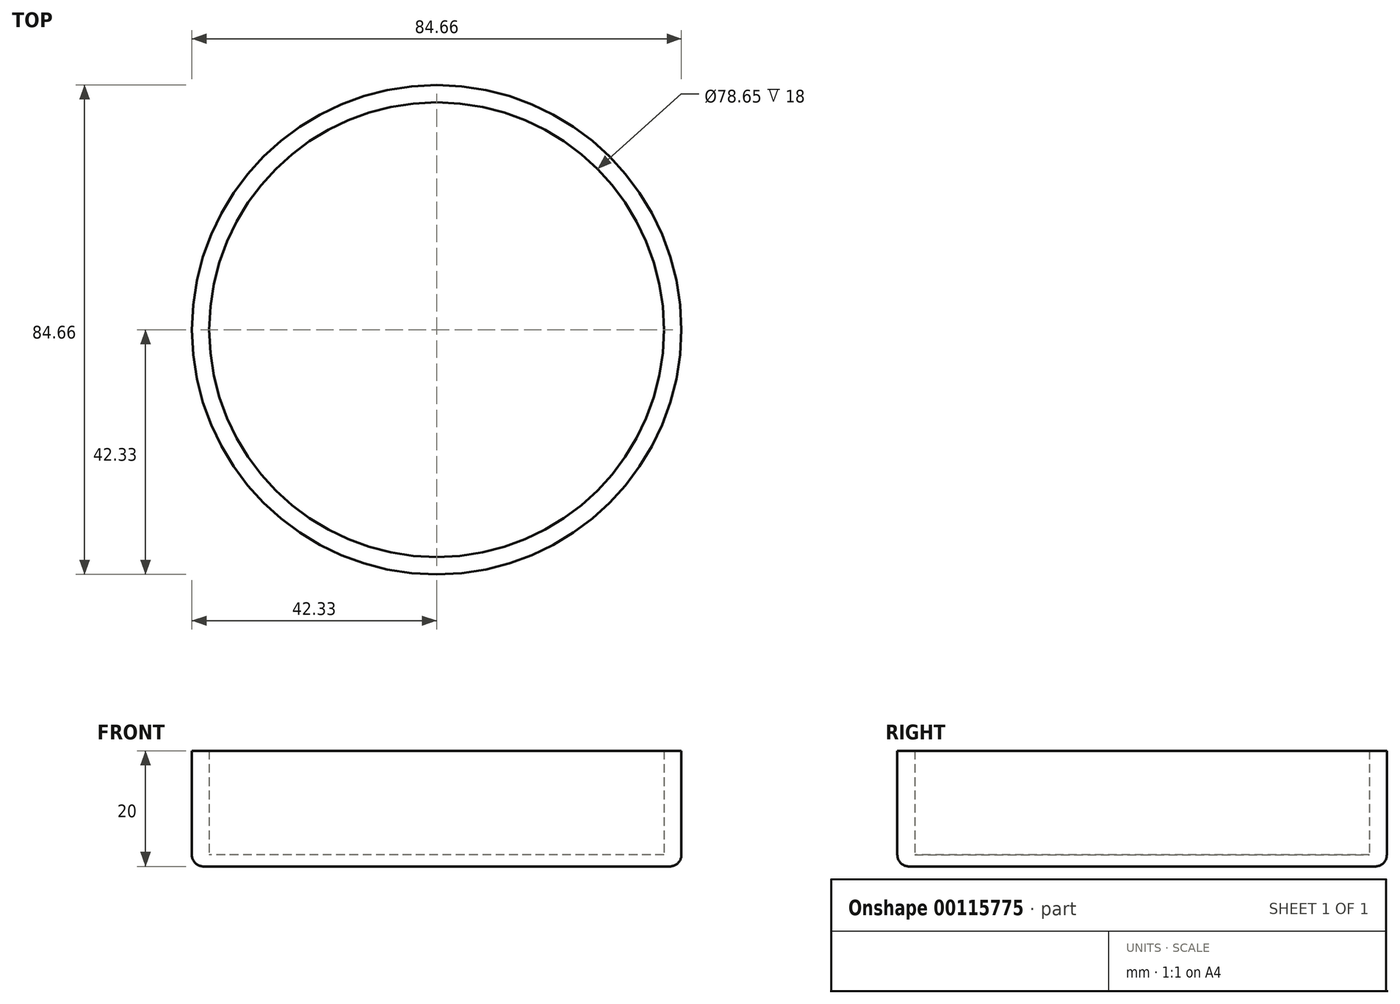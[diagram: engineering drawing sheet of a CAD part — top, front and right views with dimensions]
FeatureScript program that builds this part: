
annotation { "Feature Type Name" : "Feature", "Feature Type Description" : "" }
export const myFeature = defineFeature(function(context is Context, id is Id, definition is map)
    precondition{}
    {
        {
            var Q0;
            Q0=qCreatedBy(makeId("Top.planeOp"),FACE);
            var sketch = newSketch(context, id + "F0", { "sketchPlane" : qUnion([Q0])});
            skCircle(sketch, "E0", {"center": v(0, 0) * mm, "radius": 42.33 * mm});
            skSolve(sketch);
        }
        {
            var Q0;
            Q0=makeQuery(id+"F0.imprint","IMPRINT",FACE,{"disambiguationData":[TD([[makeQuery(id+"F0.imprint","IMPRINT",EDGE,{"derivedFrom":sQuery(id+"F0.wireOp",EDGE,"E0")}),1.0]])]});
            extrude(context, id + "F1", {"entities" : qUnion([Q0]), "depth" : 2 * mm});
        }
        {
            var Q0;
            Q0=makeQuery(id+"F1.opExtrude","CAP_FACE",FACE,{"disambiguationData":[OSD([sQuery(id+"F0.wireOp",EDGE,"E0")])],"isStart":false});
            var sketch = newSketch(context, id + "F2", { "sketchPlane" : qUnion([Q0])});
            skCircle(sketch, "E1", {"center": v(0, 0) * mm, "radius": 42.33 * mm});
            skCircle(sketch, "E2", {"center": v(0, 0) * mm, "radius": 39.33 * mm});
            skSolve(sketch);
        }
        {
            var Q0;
            Q0=makeQuery(id+"F2.imprint","IMPRINT",FACE,{"disambiguationData":[TD([[makeQuery(id+"F2.imprint","IMPRINT",EDGE,{"derivedFrom":sQuery(id+"F2.wireOp",EDGE,"E1")}),1.0]])]});
            extrude(context, id + "F3", {"entities" : qUnion([Q0]), "operationType" : NewBodyOperationType.ADD, "depth" : 18 * mm});
        }
        {
            var Q0;
            Q0=makeQuery(id+"F1.opExtrude","CAP_EDGE",EDGE,{"disambiguationData":[OSD([sQuery(id+"F0.wireOp",EDGE,"E0")])],"isStart":true});
            fillet(context, id + "F4", {"entities" : qUnion([Q0]), "radius" : 2 * mm, "tangentPropagation" : true, "allowEdgeOverflow" : false});
        }
    });
